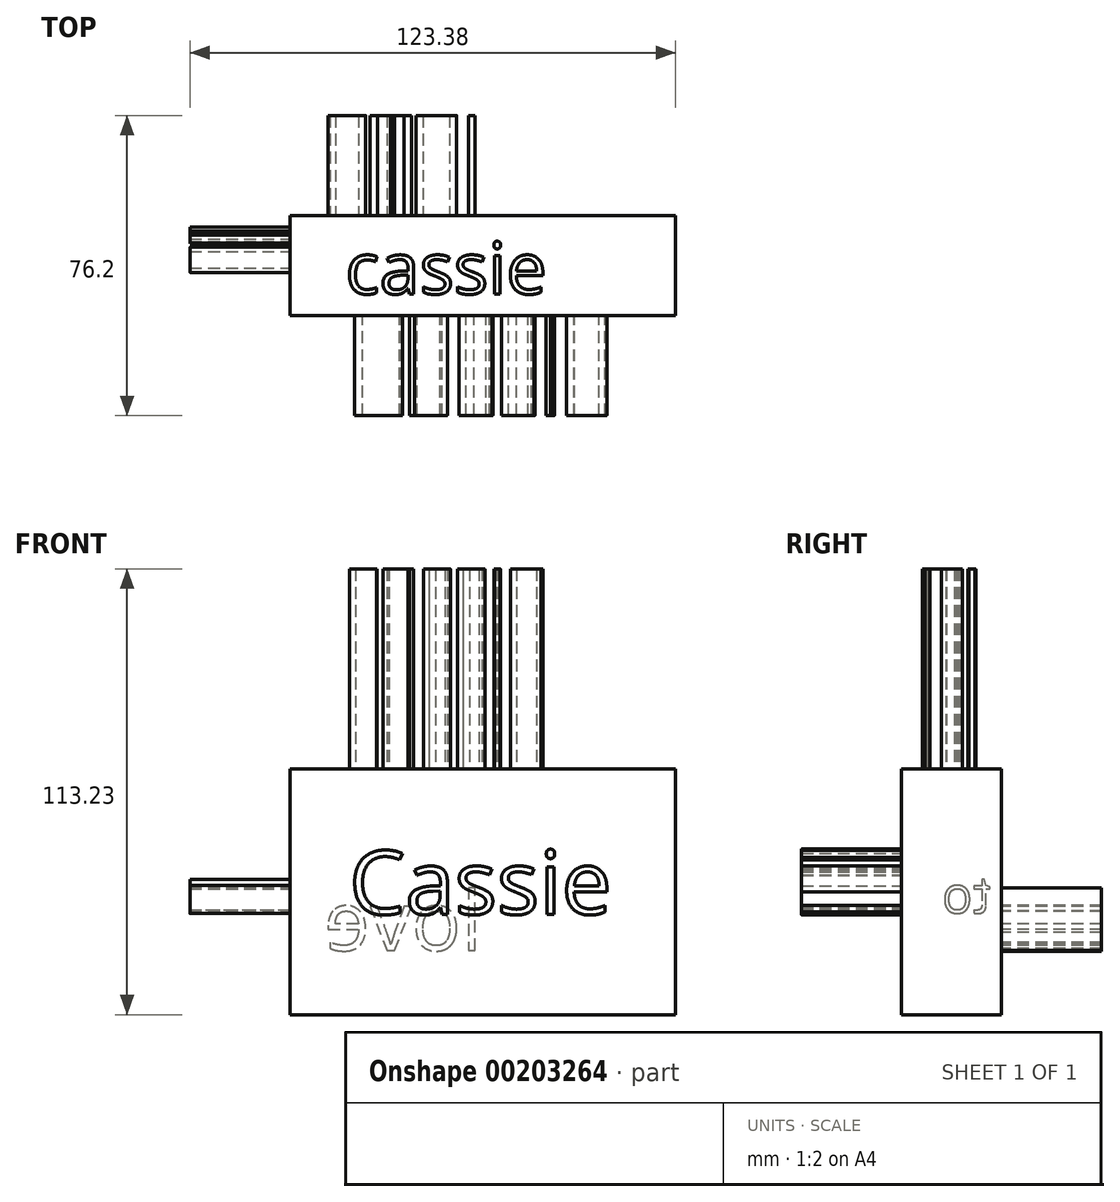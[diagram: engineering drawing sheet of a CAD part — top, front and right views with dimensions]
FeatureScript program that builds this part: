
annotation { "Feature Type Name" : "Feature", "Feature Type Description" : "" }
export const myFeature = defineFeature(function(context is Context, id is Id, definition is map)
    precondition{}
    {
        {
            var Q0;
            Q0=qCreatedBy(makeId("Front.planeOp"),FACE);
            var sketch = newSketch(context, id + "F0", { "sketchPlane" : qUnion([Q0])});
            skLineSegment(sketch, "E0.bottom", {"start": v(-28.6, 40.2) * mm, "end": v(69.38, 40.2) * mm});
            skLineSegment(sketch, "E0.top", {"start": v(-28.6, -22.23) * mm, "end": v(69.38, -22.23) * mm});
            skLineSegment(sketch, "E0.left", {"start": v(-28.6, 40.2) * mm, "end": v(-28.6, -22.23) * mm});
            skLineSegment(sketch, "E0.right", {"start": v(69.38, 40.2) * mm, "end": v(69.38, -22.23) * mm});
            skSolve(sketch);
        }
        {
            var Q0;
            Q0 = qSketchRegion(id + "F0", true);
            extrude(context, id + "F1", {"entities" : qUnion([Q0]), "depth" : 25.4 * mm});
        }
        {
            var Q0;
            Q0=makeQuery(id+"F1.opExtrude","CAP_FACE",FACE,{"disambiguationData":[OSD([sQuery(id+"F0.wireOp",EDGE,"E0.bottom"),sQuery(id+"F0.wireOp",EDGE,"E0.top"),sQuery(id+"F0.wireOp",EDGE,"E0.left"),sQuery(id+"F0.wireOp",EDGE,"E0.right")])],"isStart":false});
            var sketch = newSketch(context, id + "F2", { "sketchPlane" : qUnion([Q0])});
            skText(sketch, "E1", { "text": "Cassie", "fontName": "OpenSans-Regular.ttf"});
            const initialGuessF2  = {"E1": [-0.01353, 0.00329, 1, 0, 0.01623]};
            skSetInitialGuess(sketch, initialGuessF2);
            skSolve(sketch);
        }
        {
            var Q0;
            Q0 = qSketchRegion(id + "F2", true);
            extrude(context, id + "F3", {"entities" : qUnion([Q0]), "operationType" : NewBodyOperationType.ADD, "depth" : 25.4 * mm});
        }
        {
            var Q0;
            Q0=makeQuery(id+"F1.opExtrude","CAP_FACE",FACE,{"disambiguationData":[OSD([sQuery(id+"F0.wireOp",EDGE,"E0.bottom"),sQuery(id+"F0.wireOp",EDGE,"E0.top"),sQuery(id+"F0.wireOp",EDGE,"E0.left"),sQuery(id+"F0.wireOp",EDGE,"E0.right")])],"isStart":true});
            var sketch = newSketch(context, id + "F4", { "sketchPlane" : qUnion([Q0])});
            skText(sketch, "E2", { "text": "love", "fontName": "OpenSans-Regular.ttf"});
            const initialGuessF4  = {"E2": [-0.02021, -0.0059, 1, 0, 0.01507]};
            skSetInitialGuess(sketch, initialGuessF4);
            skSolve(sketch);
        }
        {
            var Q0;
            Q0 = qSketchRegion(id + "F4", true);
            extrude(context, id + "F5", {"entities" : qUnion([Q0]), "operationType" : NewBodyOperationType.ADD, "depth" : 25.4 * mm});
        }
        {
            var Q0;
            Q0=makeQuery(id+"F1.opExtrude","SWEPT_FACE",FACE,{"disambiguationData":[OSD([sQuery(id+"F0.wireOp",EDGE,"E0.bottom")])]});
            var sketch = newSketch(context, id + "F6", { "sketchPlane" : qUnion([Q0])});
            skText(sketch, "E3", { "text": "cassie", "fontName": "OpenSans-Regular.ttf"});
            const initialGuessF6  = {"E3": [-0.0145, -0.0199, 1, 0, 0.01314]};
            skSetInitialGuess(sketch, initialGuessF6);
            skSolve(sketch);
        }
        {
            var Q0;
            Q0 = qSketchRegion(id + "F6", true);
            extrude(context, id + "F7", {"entities" : qUnion([Q0]), "operationType" : NewBodyOperationType.ADD, "depth" : 50.8 * mm});
        }
        {
            var Q0;
            Q0=makeQuery(id+"F1.opExtrude","SWEPT_FACE",FACE,{"disambiguationData":[OSD([sQuery(id+"F0.wireOp",EDGE,"E0.left")])]});
            var sketch = newSketch(context, id + "F8", { "sketchPlane" : qUnion([Q0])});
            skText(sketch, "E4", { "text": "to", "fontName": "OpenSans-Regular.ttf"});
            const initialGuessF8  = {"E4": [0.00276, 0.00358, 1, 0, 0.00933]};
            skSetInitialGuess(sketch, initialGuessF8);
            skSolve(sketch);
        }
        {
            var Q0;
            Q0 = qSketchRegion(id + "F8", true);
            extrude(context, id + "F9", {"entities" : qUnion([Q0]), "operationType" : NewBodyOperationType.ADD, "depth" : 25.4 * mm});
        }
    });
